# Revit family: COTTO-ฝักบัวพร้อมสาย 3 ฟังก์ชั่น-ZH018(HM)
name_source: partatom
category: Plumbing Fixtures
revit_build: Autodesk Revit 2017 (Build: 20160720_1515(x64)
units: mm (PartAtom-declared; Revit-internal decimal feet)

## family parameters
Always vertical = Yes
Cut with Voids When Loaded = No
Part Type = Normal
Room Calculation Point = No
Round Connector Dimension = Use Diameter
Shared = No
Work Plane-Based = No

## types (1)
- COTTO-ฝักบัวพร้อมสาย 3 ฟังก์ชั่น-ZH018(HM)
    Barcode = 8852410900867
    CW Connection = No
    Code = ZH018(HM)
    Color = โครเมี่ยม
    Description = ฝักบัวพร้อมสาย 3 ฟังก์ชั่น
    Drain = 0 mm  [stored 0 ft]
    Manufacturer = COTTO
    Material = SCG พลาสติก ABS
    Sap Code = Z234ZH018HMXXXXX11
    Standard = มอก. 2066-2552
    URL = https://www.cotto.com
    Waste Connection = No
    Water Supply = 0 mm  [stored 0 ft]
    กว้าง (มม.) = 12 mm  [stored 0.0393701 ft]
    น้ำหนัก (kg.) = 0.7
    ยาว (มม.) = 0 mm  [stored 0 ft]
    รูปแบบการติดตั้ง = ติดบนผนัง
    สูง (มม.) = 27 mm
    แรงดันน้ำ = 3 บาร์

note: [stored X ft] marks values corroborated as IEEE doubles in the binary element streams (Revit-internal decimal feet)

## geometry (parser evidence)
native form markers: Sweep x3
no freeform markers — native parametric forms only
